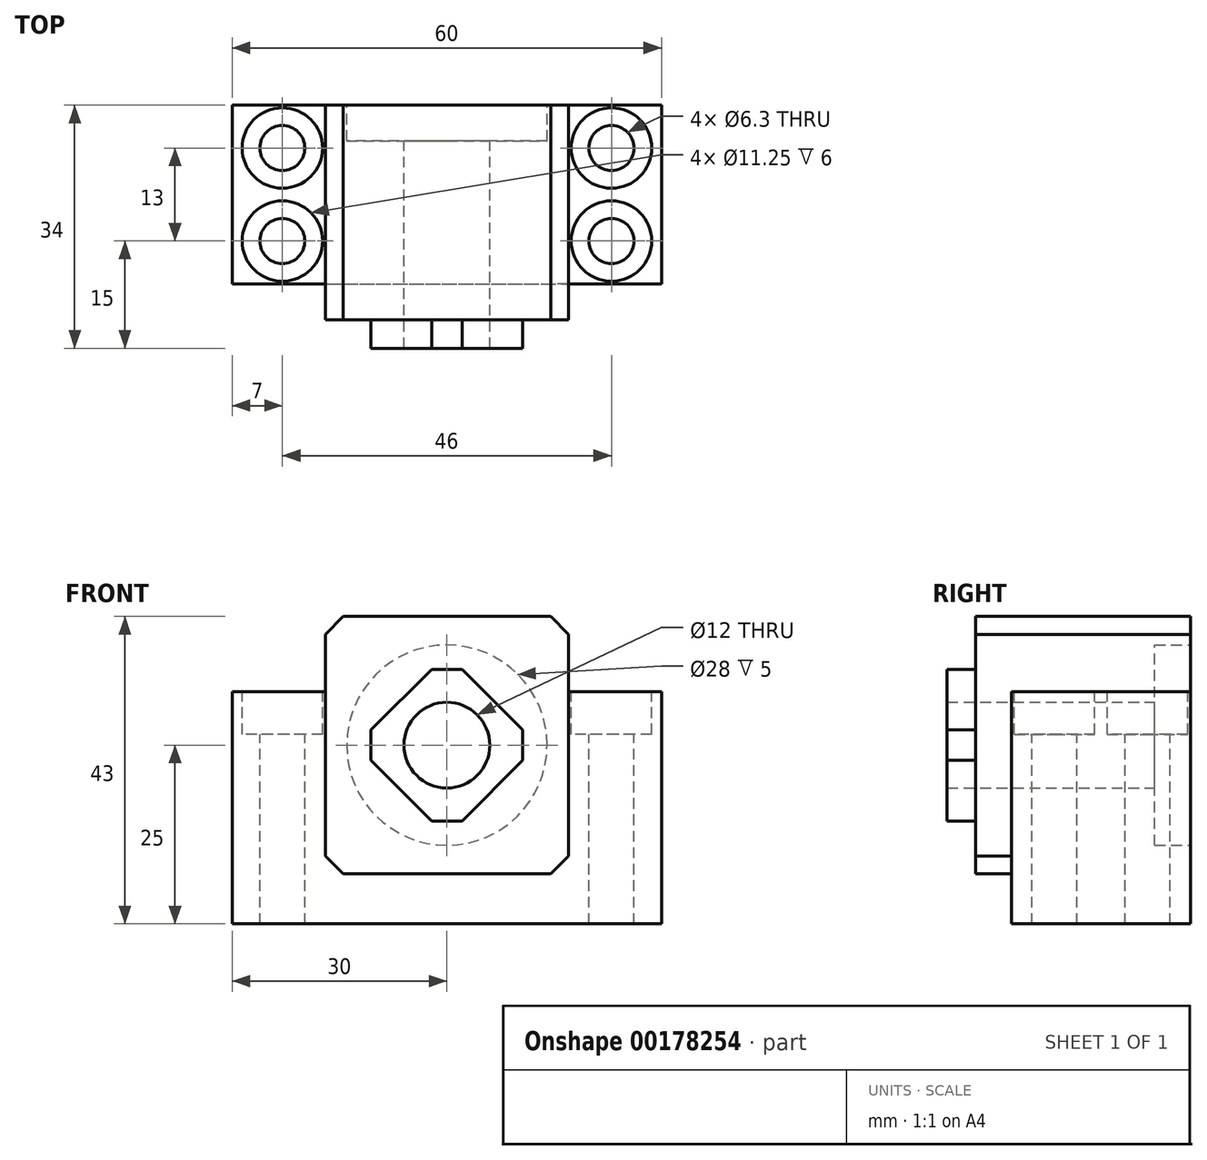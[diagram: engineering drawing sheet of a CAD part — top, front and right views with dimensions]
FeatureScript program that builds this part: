
annotation { "Feature Type Name" : "Feature", "Feature Type Description" : "" }
export const myFeature = defineFeature(function(context is Context, id is Id, definition is map)
    precondition{}
    {
        {
            var Q0;
            Q0=qCreatedBy(makeId("Front.planeOp"),FACE);
            var sketch = newSketch(context, id + "F0", { "sketchPlane" : qUnion([Q0])});
            skLineSegment(sketch, "E0.bottom", {"start": v(-30, -16.25) * mm, "end": v(30, -16.25) * mm});
            skLineSegment(sketch, "E0.top", {"start": v(-30, 16.25) * mm, "end": v(-17, 16.25) * mm});
            skLineSegment(sketch, "E0.left", {"start": v(-30, -16.25) * mm, "end": v(-30, 16.25) * mm});
            skLineSegment(sketch, "E0.right", {"start": v(30, -16.25) * mm, "end": v(30, 16.25) * mm});
            skPoint(sketch, "E0.middle", {"position": v(0, 0) * mm});
            skLineSegment(sketch, "E1.bottom", {"start": v(-17, 26.75) * mm, "end": v(17, 26.75) * mm});
            skLineSegment(sketch, "E1.left", {"start": v(-17, 26.75) * mm, "end": v(-17, 16.25) * mm});
            skLineSegment(sketch, "E1.right", {"start": v(17, 26.75) * mm, "end": v(17, 16.25) * mm});
            skLineSegment(sketch, "E2.trimOffspring", {"start": v(17, 16.25) * mm, "end": v(30, 16.25) * mm});
            skLineSegment(sketch, "E3", {"start": v(0, 26.75) * mm, "end": v(0, -16.25) * mm, "construction": true});
            skLineSegment(sketch, "E4", {"start": v(-30, 8.75) * mm, "end": v(30, 8.75) * mm, "construction": true});
            skCircle(sketch, "E5", {"center": v(0, 8.75) * mm, "radius": 6 * mm});
            skCircle(sketch, "E6", {"center": v(0, 8.75) * mm, "radius": 14 * mm});
            skSolve(sketch);
        }
        {
            var Q0;
            Q0=makeQuery(id+"F0.imprint","IMPRINT",FACE,{"disambiguationData":[TD([[makeQuery(id+"F0.imprint","IMPRINT",EDGE,{"derivedFrom":sQuery(id+"F0.wireOp",EDGE,"E0.bottom")}),1.0]])]});
            var Q1;
            Q1=makeQuery(id+"F0.imprint","IMPRINT",FACE,{"disambiguationData":[TD([[makeQuery(id+"F0.imprint","IMPRINT",EDGE,{"derivedFrom":sQuery(id+"F0.wireOp",EDGE,"E5")}),-1.0]])]});
            extrude(context, id + "F1", {"entities" : qUnion([Q0, Q1]), "depth" : 25 * mm});
        }
        {
            var Q0;
            Q0=makeQuery(id+"F1.opExtrude","SWEPT_FACE",FACE,{"disambiguationData":[OSD([sQuery(id+"F0.wireOp",EDGE,"E2.trimOffspring")])]});
            var sketch = newSketch(context, id + "F2", { "sketchPlane" : qUnion([Q0])});
            skLineSegment(sketch, "E7", {"start": v(23, -25) * mm, "end": v(23, 0) * mm, "construction": true});
            skLineSegment(sketch, "E8", {"start": v(-23, -25) * mm, "end": v(-23, 0) * mm, "construction": true});
            skLineSegment(sketch, "E9", {"start": v(0, 0) * mm, "end": v(0, -25) * mm, "construction": true});
            skLineSegment(sketch, "E10", {"start": v(30, -6) * mm, "end": v(-30, -6) * mm, "construction": true});
            skLineSegment(sketch, "E11", {"start": v(30, -19) * mm, "end": v(-30, -19) * mm, "construction": true});
            skPoint(sketch, "E12", {"position": v(-23, -6) * mm});
            skPoint(sketch, "E13", {"position": v(-23, -19) * mm});
            skPoint(sketch, "E14", {"position": v(23, -6) * mm});
            skPoint(sketch, "E15", {"position": v(23, -19) * mm});
            skSolve(sketch);
        }
        {
            var Q0;
            Q0=sQuery(id+"F2.wireOp",VERTEX,"10969605-896d-48e8-a0ea-adc1b2655bab");
            var Q1;
            Q1=sQuery(id+"F2.wireOp",VERTEX,"42efcb25-5196-4f44-a0df-db42c3beecd8.positionSnap0");
            var Q2;
            Q2=sQuery(id+"F2.wireOp",VERTEX,"E12");
            var Q3;
            Q3=sQuery(id+"F2.wireOp",VERTEX,"E13");
            var Q4;
            Q4=sQuery(id+"F2.wireOp",VERTEX,"E14");
            var Q5;
            Q5=sQuery(id+"F2.wireOp",VERTEX,"E15");
            var Q6;
            Q6=makeQuery(id+"F1.opExtrude","SWEPT_BODY",BODY,{"disambiguationData":[OSD([sQuery(id+"F0.wireOp",EDGE,"E0.bottom"),sQuery(id+"F0.wireOp",EDGE,"E0.top"),sQuery(id+"F0.wireOp",EDGE,"E0.left"),sQuery(id+"F0.wireOp",EDGE,"E0.right"),sQuery(id+"F0.wireOp",EDGE,"E1.bottom"),sQuery(id+"F0.wireOp",EDGE,"E1.left"),sQuery(id+"F0.wireOp",EDGE,"E1.right"),sQuery(id+"F0.wireOp",EDGE,"E2.trimOffspring"),sQuery(id+"F0.wireOp",EDGE,"E5")])]});
            hole(context, id + "F3", {"style" : HoleStyle.C_BORE, "endStyle" : HoleEndStyle.THROUGH, "standardTappedOrClearance" : lookupTablePath({ "standard" : "ISO", "fit" : "Close", "size" : "M6", "type" : "Clearance" }), "standardBlindInLast" : lookupTablePath({ "fit" : "Close", "standard" : "ISO", "size" : "M6", "type" : "Clearance" }), "holeDiameter" : 6.3 * mm, "cBoreDiameter" : 11.25 * mm, "cBoreDepth" : 6 * mm, "locations" : qUnion([Q0, Q1, Q2, Q3, Q4, Q5]), "scope" : qUnion([Q6]), "isTappedThrough" : true});
        }
        {
            var Q0;
            Q0=makeQuery(id+"F1.opExtrude","SWEPT_EDGE",EDGE,{"disambiguationData":[OSD([sQuery(id+"F0.wireOp",EDGE,"E1.bottom"),sQuery(id+"F0.wireOp",EDGE,"E1.right")])]});
            var Q1;
            Q1=makeQuery(id+"F1.opExtrude","SWEPT_EDGE",EDGE,{"disambiguationData":[OSD([sQuery(id+"F0.wireOp",EDGE,"E1.bottom"),sQuery(id+"F0.wireOp",EDGE,"E1.left")])]});
            chamfer(context, id + "F4", {"entities" : qUnion([Q0, Q1]), "width" : 2.5 * mm, "tangentPropagation" : true});
        }
        {
            var Q0;
            Q0=makeQuery(id+"F1.opExtrude","CAP_FACE",FACE,{"disambiguationData":[OSD([sQuery(id+"F0.wireOp",EDGE,"E0.bottom"),sQuery(id+"F0.wireOp",EDGE,"E0.top"),sQuery(id+"F0.wireOp",EDGE,"E0.left"),sQuery(id+"F0.wireOp",EDGE,"E0.right"),sQuery(id+"F0.wireOp",EDGE,"E1.bottom"),sQuery(id+"F0.wireOp",EDGE,"E1.left"),sQuery(id+"F0.wireOp",EDGE,"E1.right"),sQuery(id+"F0.wireOp",EDGE,"E2.trimOffspring"),sQuery(id+"F0.wireOp",EDGE,"E5")])],"isStart":false});
            var sketch = newSketch(context, id + "F5", { "sketchPlane" : qUnion([Q0])});
            skLineSegment(sketch, "E16.bottom", {"start": v(-17, 26.75) * mm, "end": v(17, 26.75) * mm});
            skLineSegment(sketch, "E16.top", {"start": v(-17, -9.25) * mm, "end": v(17, -9.25) * mm});
            skLineSegment(sketch, "E16.left", {"start": v(-17, 26.75) * mm, "end": v(-17, -9.25) * mm});
            skLineSegment(sketch, "E16.right", {"start": v(17, 26.75) * mm, "end": v(17, -9.25) * mm});
            skPoint(sketch, "E16.middle", {"position": v(0, 8.75) * mm});
            skCircle(sketch, "E17", {"center": v(0, 8.75) * mm, "radius": 6 * mm});
            skSolve(sketch);
        }
        {
            var Q0;
            Q0=qSketchRegion(id+"F5",true);
            extrude(context, id + "F6", {"entities" : qUnion([Q0]), "operationType" : NewBodyOperationType.ADD, "depth" : 5 * mm});
        }
        {
            var Q0;
            Q0=makeQuery(id+"F6.opExtrude","SWEPT_EDGE",EDGE,{"disambiguationData":[OSD([sQuery(id+"F5.wireOp",EDGE,"E16.bottom"),sQuery(id+"F5.wireOp",EDGE,"E16.right")])]});
            var Q1;
            Q1=makeQuery(id+"F6.opExtrude","SWEPT_EDGE",EDGE,{"disambiguationData":[OSD([sQuery(id+"F5.wireOp",EDGE,"E16.bottom"),sQuery(id+"F5.wireOp",EDGE,"E16.left")])]});
            var Q2;
            Q2=makeQuery(id+"F6.opExtrude","SWEPT_EDGE",EDGE,{"disambiguationData":[OSD([sQuery(id+"F5.wireOp",EDGE,"E16.top"),sQuery(id+"F5.wireOp",EDGE,"E16.right")])]});
            var Q3;
            Q3=makeQuery(id+"F6.opExtrude","SWEPT_EDGE",EDGE,{"disambiguationData":[OSD([sQuery(id+"F5.wireOp",EDGE,"E16.top"),sQuery(id+"F5.wireOp",EDGE,"E16.left")])]});
            chamfer(context, id + "F7", {"entities" : qUnion([Q0, Q1, Q2, Q3]), "width" : 2.5 * mm, "tangentPropagation" : true});
        }
        {
            var Q0;
            Q0=makeQuery(id+"F6.opExtrude","CAP_FACE",FACE,{"disambiguationData":[OSD([sQuery(id+"F5.wireOp",EDGE,"E16.bottom"),sQuery(id+"F5.wireOp",EDGE,"E16.top"),sQuery(id+"F5.wireOp",EDGE,"E16.left"),sQuery(id+"F5.wireOp",EDGE,"E16.right"),sQuery(id+"F5.wireOp",EDGE,"E17")])],"isStart":false});
            var sketch = newSketch(context, id + "F8", { "sketchPlane" : qUnion([Q0])});
            skCircle(sketch, "E18.cCircle", {"center": v(0, 8.75) * mm, "radius": 12.73 * mm, "construction": true});
            skPoint(sketch, "E18.cCircle.perimeterSnap0", {"position": v(-17, 8.75) * mm});
            skLineSegment(sketch, "E18.0", {"start": v(-12.73, 8.75) * mm, "end": v(0, 21.48) * mm});
            skPoint(sketch, "E18.0.startSnap0", {"position": v(-17, 8.75) * mm});
            skLineSegment(sketch, "E18.1", {"start": v(0, 21.48) * mm, "end": v(12.73, 8.75) * mm});
            skLineSegment(sketch, "E18.2", {"start": v(12.73, 8.75) * mm, "end": v(0, -3.98) * mm});
            skLineSegment(sketch, "E18.3", {"start": v(0, -3.98) * mm, "end": v(-12.73, 8.75) * mm});
            skSolve(sketch);
        }
        {
            var Q0;
            Q0=makeQuery(id+"F8.imprint","IMPRINT",FACE,{"disambiguationData":[TD([[makeQuery(id+"F8.imprint","IMPRINT",EDGE,{"derivedFrom":sQuery(id+"F8.wireOp",EDGE,"E18.0")}),-1.0]])]});
            extrude(context, id + "F9", {"entities" : qUnion([Q0]), "operationType" : NewBodyOperationType.ADD, "depth" : 4 * mm});
        }
        {
            var Q0;
            Q0=makeQuery(id+"F9.opExtrude","SWEPT_EDGE",EDGE,{"disambiguationData":[OSD([sQuery(id+"F8.wireOp",EDGE,"E18.0"),sQuery(id+"F8.wireOp",EDGE,"E18.1")])]});
            var Q1;
            Q1=makeQuery(id+"F9.opExtrude","SWEPT_EDGE",EDGE,{"disambiguationData":[OSD([sQuery(id+"F8.wireOp",EDGE,"E18.1"),sQuery(id+"F8.wireOp",EDGE,"E18.2")])]});
            var Q2;
            Q2=makeQuery(id+"F9.opExtrude","SWEPT_EDGE",EDGE,{"disambiguationData":[OSD([sQuery(id+"F8.wireOp",EDGE,"E18.0"),sQuery(id+"F8.wireOp",EDGE,"E18.3")])]});
            var Q3;
            Q3=makeQuery(id+"F9.opExtrude","SWEPT_EDGE",EDGE,{"disambiguationData":[OSD([sQuery(id+"F8.wireOp",EDGE,"E18.2"),sQuery(id+"F8.wireOp",EDGE,"E18.3")])]});
            chamfer(context, id + "F10", {"entities" : qUnion([Q0, Q1, Q2, Q3]), "width" : 3 * mm, "tangentPropagation" : true});
        }
        {
            var Q0;
            Q0=makeQuery(id+"F0.imprint","IMPRINT",FACE,{"disambiguationData":[TD([[makeQuery(id+"F0.imprint","IMPRINT",EDGE,{"derivedFrom":sQuery(id+"F0.wireOp",EDGE,"E5")}),-1.0]])]});
            extrude(context, id + "F11", {"entities" : qUnion([Q0]), "operationType" : NewBodyOperationType.REMOVE, "depth" : 5 * mm});
        }
    });
